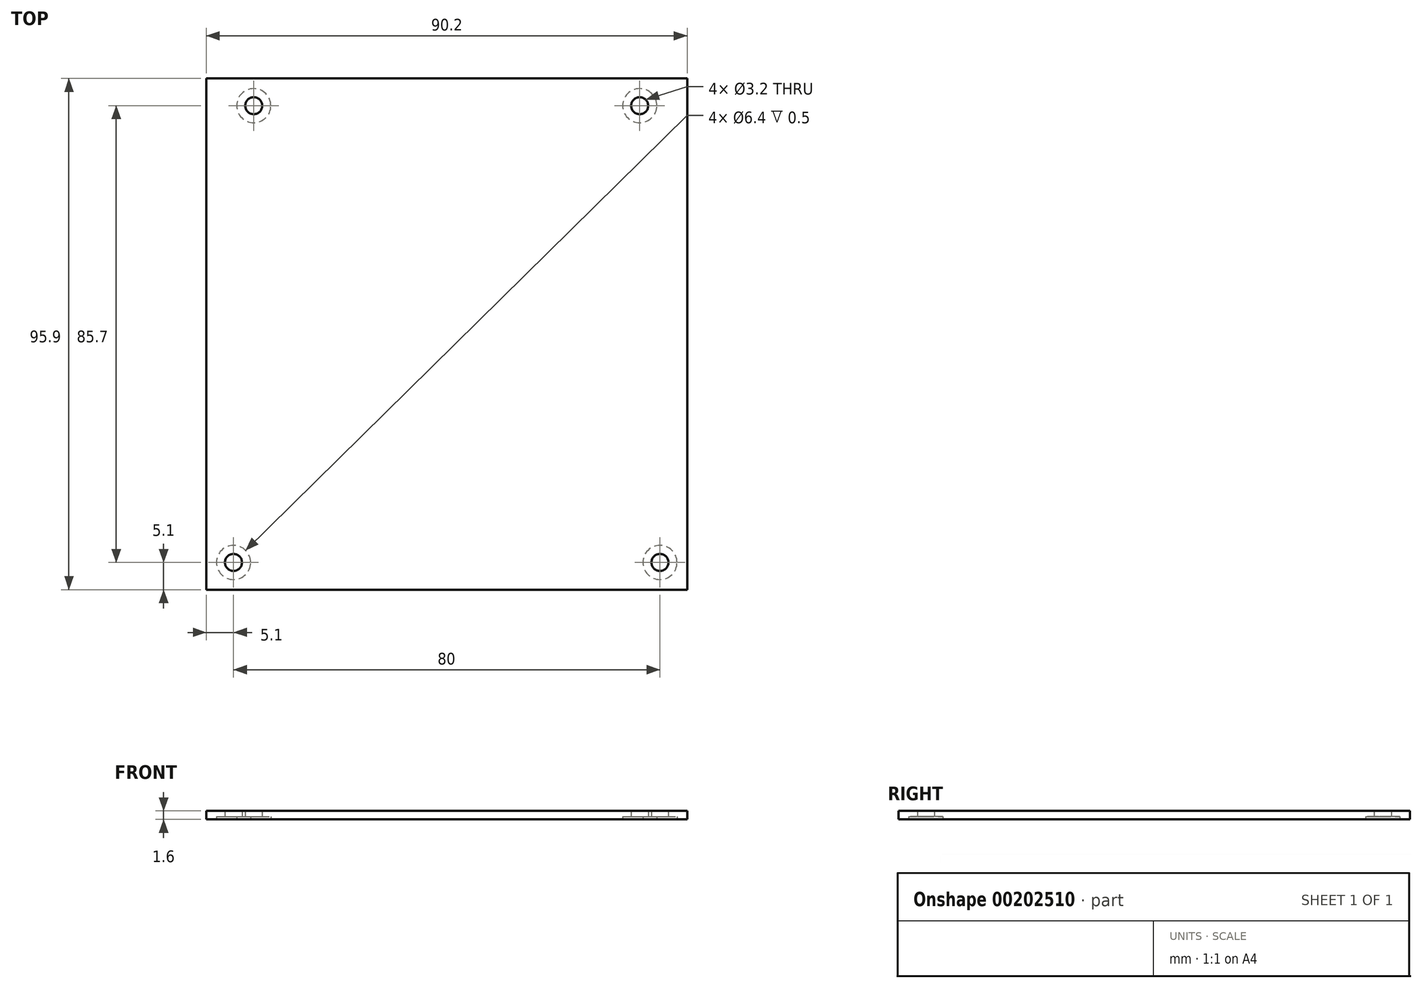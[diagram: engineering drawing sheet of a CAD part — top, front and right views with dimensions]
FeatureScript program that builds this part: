
annotation { "Feature Type Name" : "Feature", "Feature Type Description" : "" }
export const myFeature = defineFeature(function(context is Context, id is Id, definition is map)
    precondition{}
    {
        {
            var Q0;
            Q0=qCreatedBy(makeId("Top.planeOp"),FACE);
            var sketch = newSketch(context, id + "F0", { "sketchPlane" : qUnion([Q0])});
            skLineSegment(sketch, "E0.bottom", {"start": v(45.1, 47.95) * mm, "end": v(-45.1, 47.95) * mm});
            skLineSegment(sketch, "E0.top", {"start": v(45.1, -47.95) * mm, "end": v(-45.1, -47.95) * mm});
            skLineSegment(sketch, "E0.left", {"start": v(45.1, 47.95) * mm, "end": v(45.1, -47.95) * mm});
            skLineSegment(sketch, "E0.right", {"start": v(-45.1, 47.95) * mm, "end": v(-45.1, -47.95) * mm});
            skPoint(sketch, "E0.middle", {"position": v(0, 0) * mm});
            skPoint(sketch, "E1", {"position": v(-36.2, 42.85) * mm});
            skPoint(sketch, "E2", {"position": v(-40, -42.85) * mm});
            skPoint(sketch, "E3.MirrorP", {"position": v(36.2, 42.85) * mm});
            skPoint(sketch, "E4.MirrorP", {"position": v(40, -42.85) * mm});
            skSolve(sketch);
        }
        {
            var Q0;
            Q0 = qSketchRegion(id + "F0", true);
            extrude(context, id + "F1", {"entities" : qUnion([Q0]), "depth" : 1.6 * mm});
        }
        {
            var Q0;
            Q0=sQuery(id+"F0.wireOp",VERTEX,"E1");
            var Q1;
            Q1=makeQuery(id+"F1.opExtrude","SWEPT_BODY",BODY,{"disambiguationData":[OSD([sQuery(id+"F0.wireOp",EDGE,"E0.bottom"),sQuery(id+"F0.wireOp",EDGE,"E0.top"),sQuery(id+"F0.wireOp",EDGE,"E0.left"),sQuery(id+"F0.wireOp",EDGE,"E0.right")])]});
            hole(context, id + "F2", {"style" : HoleStyle.C_BORE, "endStyle" : HoleEndStyle.THROUGH, "oppositeDirection" : true, "holeDiameter" : 3.2 * mm, "cBoreDiameter" : 6.4 * mm, "cBoreDepth" : 0.5 * mm, "locations" : qUnion([Q0]), "scope" : qUnion([Q1]), "isTappedThrough" : true});
        }
        {
            var Q0;
            Q0=sQuery(id+"F0.wireOp",VERTEX,"E2");
            var Q1;
            Q1=makeQuery(id+"F1.opExtrude","SWEPT_BODY",BODY,{"disambiguationData":[OSD([sQuery(id+"F0.wireOp",EDGE,"E0.bottom"),sQuery(id+"F0.wireOp",EDGE,"E0.top"),sQuery(id+"F0.wireOp",EDGE,"E0.left"),sQuery(id+"F0.wireOp",EDGE,"E0.right")])]});
            hole(context, id + "F3", {"style" : HoleStyle.C_BORE, "endStyle" : HoleEndStyle.THROUGH, "oppositeDirection" : true, "holeDiameter" : 3.2 * mm, "cBoreDiameter" : 6.4 * mm, "cBoreDepth" : 0.5 * mm, "locations" : qUnion([Q0]), "scope" : qUnion([Q1]), "isTappedThrough" : true});
        }
        {
            var Q0;
            Q0=sQuery(id+"F0.wireOp",VERTEX,"E3.MirrorP");
            var Q1;
            Q1=makeQuery(id+"F1.opExtrude","SWEPT_BODY",BODY,{"disambiguationData":[OSD([sQuery(id+"F0.wireOp",EDGE,"E0.bottom"),sQuery(id+"F0.wireOp",EDGE,"E0.top"),sQuery(id+"F0.wireOp",EDGE,"E0.left"),sQuery(id+"F0.wireOp",EDGE,"E0.right")])]});
            hole(context, id + "F4", {"style" : HoleStyle.C_BORE, "endStyle" : HoleEndStyle.THROUGH, "oppositeDirection" : true, "holeDiameter" : 3.2 * mm, "cBoreDiameter" : 6.4 * mm, "cBoreDepth" : 0.5 * mm, "locations" : qUnion([Q0]), "scope" : qUnion([Q1]), "isTappedThrough" : true});
        }
        {
            var Q0;
            Q0=sQuery(id+"F0.wireOp",VERTEX,"E4.MirrorP");
            var Q1;
            Q1=makeQuery(id+"F1.opExtrude","SWEPT_BODY",BODY,{"disambiguationData":[OSD([sQuery(id+"F0.wireOp",EDGE,"E0.bottom"),sQuery(id+"F0.wireOp",EDGE,"E0.top"),sQuery(id+"F0.wireOp",EDGE,"E0.left"),sQuery(id+"F0.wireOp",EDGE,"E0.right")])]});
            hole(context, id + "F5", {"style" : HoleStyle.C_BORE, "endStyle" : HoleEndStyle.THROUGH, "oppositeDirection" : true, "holeDiameter" : 3.2 * mm, "cBoreDiameter" : 6.4 * mm, "cBoreDepth" : 0.5 * mm, "locations" : qUnion([Q0]), "scope" : qUnion([Q1]), "isTappedThrough" : true});
        }
    });
